# Revit family: NBS_DudleyIndustries_TltPprBulkDpnsrs_PlasmaRange_ToiletPaperDispenser
name_source: partatom
category: Specialty Equipment
revit_build: Autodesk Revit 2016 (Build: 20150220_1215(x64)
units: mm (PartAtom-declared; Revit-internal decimal feet)

## family parameters
Cut with Voids When Loaded = No
Host = Face
OmniClass Number = 23.40.20.21.21
OmniClass Title = Toilet Paper Dispensers
Part Type = Normal
Room Calculation Point = No
Round Connector Dimension = Use Diameter
Shared = No

## types (1)
- PlasmaRangeToiletPaperDispenser
    AssetType = Fixed
    BIMObjectName = NBS_DudleyIndustries_ToiletPaperBulkDispensers_PlasmaRange_ToiletPaperDispenser
    Category = Pr_40_70_22_90:Toilet paper dispensers
    Color = Stainless steel
    Default Elevation = 1200 mm
    Description = Stylish brushed stainless steel 2 Roll toilet paper dispenser
    DispenserCaseMaterial = NBS_Concept
    DispenserLockMaterial = NBS_Concept
    DurationUnit = year
    ExpectedLife = 5
    Finish = Brushed (77972SS), Polished (77972PS), White Powder Coated (77972WH)
    Form = Wall mounted
    IfcExportAs = IfcFurnitureType
    IfcExportType = NOTDEFINED
    MainColor = Stainless Steel
    ManufacturerName = Dudley Industries
    ManufacturerURL = www.dudleyindustries.com/
    Material = Stainless Steel
    MaterialsBody = Stainless steel
    MaterialsFinishColour = Brushed (77972SS), Polished (77972PS), White Powder Coated (77972WH)
    ModelNumber = 77972
    ModelReference = Plasma Range: Toilet Paper Dispenser
    NBSCertification = www.nationalbimlibrary.com/cert/q1kudjmj
    NBSDescription = Toilet paper bulk dispensers
    NBSReference = 45-35-72/366
    Name = ToiletPaperBulkDispensers_PlasmaRange_ToiletPaperDispenser_DudleyIndustries
    NominalDepth = 129 mm  [stored 0.423228 ft]
    NominalHeight = 330 mm
    NominalLength = 126 mm  [stored 0.413386 ft]
    NominalWidth = 126 mm  [stored 0.413386 ft]
    Operation = Pull out
    ProductInformation = www.dudleyindustries.com/wp-content/uploads/2016/11/2-Roll-Toilet-Paper-Dispenser.pdf
    Size = 126 x 330mm x 129mm
    Uniclass2015Code = Pr_40_70_22_90
    Uniclass2015Title = Toilet paper dispensers
    Uniclass2015Version = Products v1.7
    Version = 2
    WarrantyDescription = 1 year warranty
    WarrantyDurationParts = 1
    WarrantyDurationUnit = year

note: [stored X ft] marks values corroborated as IEEE doubles in the binary element streams (Revit-internal decimal feet)

## geometry (parser evidence)
native form markers: Sweep x2
no freeform markers — native parametric forms only
